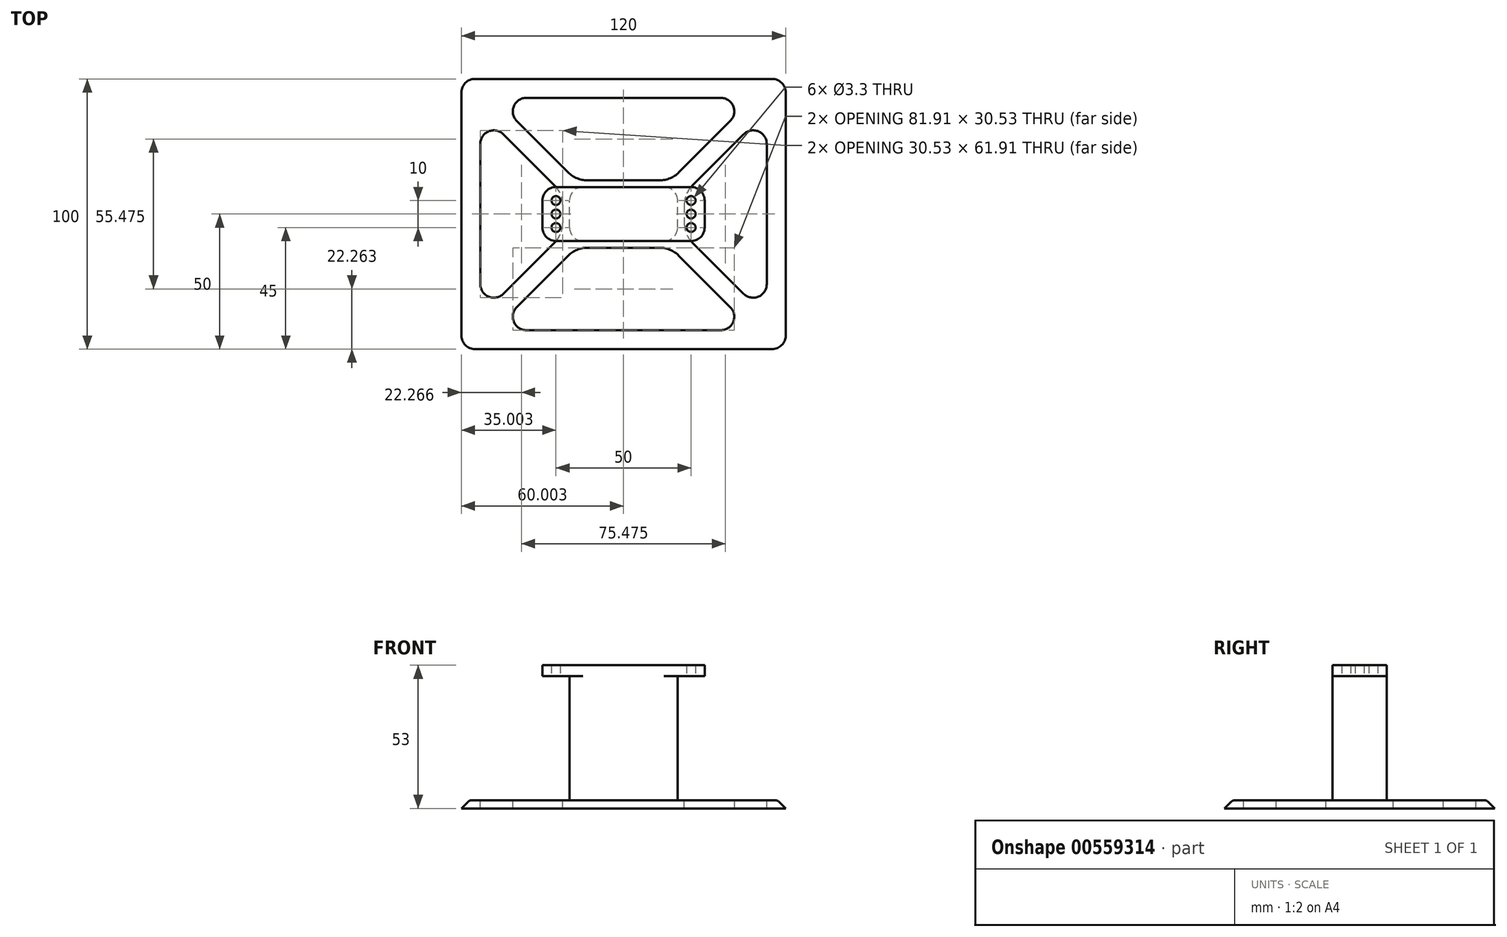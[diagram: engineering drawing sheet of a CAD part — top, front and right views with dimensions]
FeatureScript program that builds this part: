
annotation { "Feature Type Name" : "Feature", "Feature Type Description" : "" }
export const myFeature = defineFeature(function(context is Context, id is Id, definition is map)
    precondition{}
    {
        {
            var Q0;
            Q0=qCreatedBy(makeId("Top.planeOp"),FACE);
            var sketch = newSketch(context, id + "F0", { "sketchPlane" : qUnion([Q0])});
            skLineSegment(sketch, "E0", {"start": v(-14.27, 5) * mm, "end": v(35.73, 5) * mm, "construction": true});
            skLineSegment(sketch, "E1", {"start": v(35.73, 5) * mm, "end": v(35.73, 0) * mm});
            skLineSegment(sketch, "E2", {"start": v(35.73, 5) * mm, "end": v(35.73, 10) * mm});
            skLineSegment(sketch, "E3", {"start": v(-14.27, 5) * mm, "end": v(-14.27, 10) * mm});
            skLineSegment(sketch, "E4", {"start": v(-14.27, 5) * mm, "end": v(-14.27, 0) * mm});
            skLineSegment(sketch, "E5", {"start": v(-14.27, 0) * mm, "end": v(-19.27, 0) * mm, "construction": true});
            skLineSegment(sketch, "E6", {"start": v(35.73, 10) * mm, "end": v(35.73, 15) * mm, "construction": true});
            skLineSegment(sketch, "E7", {"start": v(35.73, 10) * mm, "end": v(40.73, 10) * mm, "construction": true});
            skLineSegment(sketch, "E8", {"start": v(-14.27, 0) * mm, "end": v(-14.27, -5) * mm, "construction": true});
            skLineSegment(sketch, "E9", {"start": v(-19.27, -5) * mm, "end": v(-19.27, 15) * mm});
            skLineSegment(sketch, "E10", {"start": v(-19.27, 15) * mm, "end": v(40.73, 15) * mm});
            skLineSegment(sketch, "E11", {"start": v(40.73, 15) * mm, "end": v(40.73, -5) * mm});
            skLineSegment(sketch, "E12", {"start": v(40.73, -5) * mm, "end": v(-19.27, -5) * mm});
            skCircle(sketch, "E13", {"center": v(-14.27, 10) * mm, "radius": 1.65 * mm});
            skCircle(sketch, "E14", {"center": v(-14.27, 5) * mm, "radius": 1.65 * mm});
            skCircle(sketch, "E15", {"center": v(-14.27, 0) * mm, "radius": 1.65 * mm});
            skCircle(sketch, "E16", {"center": v(35.73, 5) * mm, "radius": 1.65 * mm});
            skCircle(sketch, "E17", {"center": v(35.73, 10) * mm, "radius": 1.65 * mm});
            skCircle(sketch, "E18", {"center": v(35.73, 0) * mm, "radius": 1.65 * mm});
            skSolve(sketch);
        }
        {
            var Q0;
            Q0=makeQuery(id+"F0.imprint","IMPRINT",FACE,{"disambiguationData":[TD([[makeQuery(id+"F0.imprint","IMPRINT",EDGE,{"derivedFrom":sQuery(id+"F0.wireOp",EDGE,"E9")}),-1.0]])]});
            extrude(context, id + "F1", {"entities" : qUnion([Q0]), "depth" : 4 * mm, "offsetDistance" : 25 * mm});
        }
        {
            var Q0;
            Q0=makeQuery(id+"F1.opExtrude","CAP_FACE",FACE,{"disambiguationData":[OSD([sQuery(id+"F0.wireOp",EDGE,"E9"),sQuery(id+"F0.wireOp",EDGE,"E10"),sQuery(id+"F0.wireOp",EDGE,"E11"),sQuery(id+"F0.wireOp",EDGE,"E12"),sQuery(id+"F0.wireOp",EDGE,"E13"),sQuery(id+"F0.wireOp",EDGE,"E14"),sQuery(id+"F0.wireOp",EDGE,"E15"),sQuery(id+"F0.wireOp",EDGE,"E16"),sQuery(id+"F0.wireOp",EDGE,"E17"),sQuery(id+"F0.wireOp",EDGE,"E18")])],"isStart":true});
            var sketch = newSketch(context, id + "F2", { "sketchPlane" : qUnion([Q0])});
            skLineSegment(sketch, "E19", {"start": v(-14.27, 0) * mm, "end": v(-9.27, 0) * mm});
            skLineSegment(sketch, "E20", {"start": v(-9.27, 5) * mm, "end": v(-9.27, -15) * mm});
            skLineSegment(sketch, "E21", {"start": v(35.73, -10) * mm, "end": v(30.73, -10) * mm});
            skLineSegment(sketch, "E22", {"start": v(30.73, 5) * mm, "end": v(30.73, -15) * mm});
            skLineSegment(sketch, "E23", {"start": v(30.73, -15) * mm, "end": v(-9.27, -15) * mm});
            skLineSegment(sketch, "E24", {"start": v(-9.27, 5) * mm, "end": v(30.73, 5) * mm});
            skSolve(sketch);
        }
        {
            var Q0;
            Q0 = qSketchRegion(id + "F2", true);
            var Q1;
            {var subQ2=sQuery(id+"F2.wireOp",EDGE,"E23");Q1=makeQuery(id+"F2.imprint","IMPRINT",FACE,{"disambiguationData":[TD([[makeQuery(id+"F2.imprint","IMPRINT",EDGE,{"derivedFrom":subQ2}),1.0]])]});}
            extrude(context, id + "F3", {"entities" : qUnion([Q0, Q1]), "operationType" : NewBodyOperationType.ADD, "depth" : 46 * mm, "offsetDistance" : 25 * mm});
        }
        {
            var Q0;
            Q0=makeQuery(id+"F3.opExtrude","CAP_FACE",FACE,{"disambiguationData":[OSD([sQuery(id+"F2.wireOp",EDGE,"E20"),sQuery(id+"F2.wireOp",EDGE,"E22"),sQuery(id+"F2.wireOp",EDGE,"E23"),sQuery(id+"F2.wireOp",EDGE,"E24")])],"isStart":false});
            var sketch = newSketch(context, id + "F4", { "sketchPlane" : qUnion([Q0])});
            skLineSegment(sketch, "E25", {"start": v(30.73, 5) * mm, "end": v(70.73, 45) * mm, "construction": true});
            skLineSegment(sketch, "E26", {"start": v(10.73, 5) * mm, "end": v(10.73, -15) * mm, "construction": true});
            skLineSegment(sketch, "E27", {"start": v(30.73, -15) * mm, "end": v(70.73, -55) * mm, "construction": true});
            skLineSegment(sketch, "E28", {"start": v(70.73, 45) * mm, "end": v(70.73, -55) * mm});
            skLineSegment(sketch, "E29", {"start": v(30.73, 5) * mm, "end": v(28.26, 7.47) * mm});
            skLineSegment(sketch, "E30", {"start": v(30.73, 5) * mm, "end": v(33.2, 2.53) * mm});
            skLineSegment(sketch, "E31", {"start": v(33.2, 2.53) * mm, "end": v(70.73, 40.05) * mm});
            skLineSegment(sketch, "E32", {"start": v(30.73, -15) * mm, "end": v(33.2, -12.53) * mm});
            skLineSegment(sketch, "E33", {"start": v(30.73, -15) * mm, "end": v(28.26, -17.47) * mm});
            skLineSegment(sketch, "E34", {"start": v(33.2, -12.53) * mm, "end": v(70.73, -50.05) * mm});
            skLineSegment(sketch, "E35", {"start": v(28.26, -17.47) * mm, "end": v(65.78, -55) * mm});
            skLineSegment(sketch, "E36", {"start": v(28.26, 7.47) * mm, "end": v(65.78, 45) * mm});
            skLineSegment(sketch, "E37", {"start": v(63.73, 33.05) * mm, "end": v(70.73, 33.05) * mm, "construction": true});
            skLineSegment(sketch, "E38", {"start": v(63.73, 33.05) * mm, "end": v(63.73, -43.05) * mm});
            skLineSegment(sketch, "E39.MirrorCS", {"start": v(-9.27, -15) * mm, "end": v(-11.74, -12.53) * mm});
            skLineSegment(sketch, "E40.MirrorCS", {"start": v(-9.27, 5) * mm, "end": v(-11.74, 2.53) * mm});
            skLineSegment(sketch, "E41.MirrorCS", {"start": v(-9.27, -15) * mm, "end": v(-6.8, -17.47) * mm});
            skLineSegment(sketch, "E42.MirrorCS", {"start": v(-9.27, 5) * mm, "end": v(-6.8, 7.47) * mm});
            skLineSegment(sketch, "E43.MirrorCS", {"start": v(-42.27, 33.05) * mm, "end": v(-49.27, 33.05) * mm, "construction": true});
            skLineSegment(sketch, "E44.MirrorCS", {"start": v(-49.27, 45) * mm, "end": v(-49.27, -55) * mm});
            skLineSegment(sketch, "E45.MirrorCS", {"start": v(-6.8, 7.47) * mm, "end": v(-44.32, 45) * mm});
            skLineSegment(sketch, "E46.MirrorCS", {"start": v(-9.27, -15) * mm, "end": v(-49.27, -55) * mm, "construction": true});
            skLineSegment(sketch, "E47.MirrorCS", {"start": v(-11.74, -12.53) * mm, "end": v(-49.27, -50.05) * mm});
            skLineSegment(sketch, "E48.MirrorCS", {"start": v(-9.27, 5) * mm, "end": v(-49.27, 45) * mm, "construction": true});
            skLineSegment(sketch, "E49.MirrorCS", {"start": v(-6.8, -17.47) * mm, "end": v(-44.32, -55) * mm});
            skLineSegment(sketch, "E50.MirrorCS", {"start": v(-42.27, 33.05) * mm, "end": v(-42.27, -43.05) * mm});
            skLineSegment(sketch, "E51.MirrorCS", {"start": v(-11.74, 2.53) * mm, "end": v(-49.27, 40.05) * mm});
            skLineSegment(sketch, "E52", {"start": v(70.73, 45) * mm, "end": v(-49.27, 45) * mm});
            skLineSegment(sketch, "E53", {"start": v(-49.27, -55) * mm, "end": v(70.73, -55) * mm});
            skLineSegment(sketch, "E54", {"start": v(-6.8, 7.47) * mm, "end": v(28.26, 7.47) * mm});
            skLineSegment(sketch, "E55", {"start": v(28.26, -17.47) * mm, "end": v(-6.8, -17.47) * mm});
            skLineSegment(sketch, "E56", {"start": v(-11.74, -12.53) * mm, "end": v(-11.74, 2.53) * mm});
            skLineSegment(sketch, "E57", {"start": v(33.2, -12.53) * mm, "end": v(33.2, 2.53) * mm});
            skLineSegment(sketch, "E58", {"start": v(-37.32, 38) * mm, "end": v(-37.32, 45) * mm});
            skLineSegment(sketch, "E59", {"start": v(58.78, -55) * mm, "end": v(58.78, -48) * mm});
            skLineSegment(sketch, "E60", {"start": v(58.78, -48) * mm, "end": v(-37.32, -48) * mm});
            skLineSegment(sketch, "E61", {"start": v(-37.32, 38) * mm, "end": v(58.78, 38) * mm});
            skSolve(sketch);
        }
        {
            var Q0;
            Q0 = qSketchRegion(id + "F4", true);
            var Q1;
            Q1=makeQuery(id+"F4.imprint","IMPRINT",FACE,{"disambiguationData":[TD([[makeQuery(id+"F4.imprint","IMPRINT",EDGE,{"derivedFrom":makeQuery(id+"F3.opExtrude","CAP_EDGE",EDGE,{"disambiguationData":[OSD([sQuery(id+"F2.wireOp",EDGE,"E20")])],"isStart":false})}),1.0]])]});
            var Q2;
            Q2=makeQuery(id+"F4.imprint","IMPRINT",FACE,{"disambiguationData":[TD([[makeQuery(id+"F4.imprint","IMPRINT",EDGE,{"derivedFrom":sQuery(id+"F4.wireOp",EDGE,"E29")}),1.0]])]});
            var Q3;
            Q3=makeQuery(id+"F4.imprint","IMPRINT",FACE,{"disambiguationData":[TD([[makeQuery(id+"F4.imprint","IMPRINT",EDGE,{"derivedFrom":sQuery(id+"F4.wireOp",EDGE,"E33")}),-1.0]])]});
            var Q4;
            Q4=makeQuery(id+"F4.imprint","IMPRINT",FACE,{"disambiguationData":[TD([[makeQuery(id+"F4.imprint","IMPRINT",EDGE,{"derivedFrom":sQuery(id+"F4.wireOp",EDGE,"E39.MirrorCS")}),-1.0]])]});
            var Q5;
            Q5=makeQuery(id+"F4.imprint","IMPRINT",FACE,{"disambiguationData":[TD([[makeQuery(id+"F4.imprint","IMPRINT",EDGE,{"derivedFrom":sQuery(id+"F4.wireOp",EDGE,"E30")}),-1.0]])]});
            extrude(context, id + "F5", {"entities" : qUnion([Q0, Q1, Q2, Q3, Q4, Q5]), "operationType" : NewBodyOperationType.ADD, "depth" : 3 * mm, "offsetDistance" : 25 * mm});
        }
        {
            var Q0;
            Q0=makeQuery(id+"F3.opExtrude","CAP_EDGE",EDGE,{"disambiguationData":[OSD([sQuery(id+"F2.wireOp",EDGE,"E23")])],"isStart":false});
            var Q1;
            Q1=makeQuery(id+"F3.opExtrude","CAP_EDGE",EDGE,{"disambiguationData":[OSD([sQuery(id+"F2.wireOp",EDGE,"E22")])],"isStart":false});
            var Q2;
            Q2=makeQuery(id+"F3.opExtrude","CAP_EDGE",EDGE,{"disambiguationData":[OSD([sQuery(id+"F2.wireOp",EDGE,"E20")])],"isStart":false});
            var Q3;
            Q3=makeQuery(id+"F3.opExtrude","CAP_EDGE",EDGE,{"disambiguationData":[OSD([sQuery(id+"F2.wireOp",EDGE,"E24")])],"isStart":false});
            var Q4;
            Q4=makeQuery(id+"F1.opExtrude","SWEPT_EDGE",EDGE,{"disambiguationData":[OSD([sQuery(id+"F0.wireOp",EDGE,"E11"),sQuery(id+"F0.wireOp",EDGE,"E12")])]});
            var Q5;
            Q5=makeQuery(id+"F1.opExtrude","SWEPT_EDGE",EDGE,{"disambiguationData":[OSD([sQuery(id+"F0.wireOp",EDGE,"E10"),sQuery(id+"F0.wireOp",EDGE,"E11")])]});
            var Q6;
            Q6=makeQuery(id+"F1.opExtrude","SWEPT_EDGE",EDGE,{"disambiguationData":[OSD([sQuery(id+"F0.wireOp",EDGE,"E9"),sQuery(id+"F0.wireOp",EDGE,"E10")])]});
            var Q7;
            Q7=makeQuery(id+"F1.opExtrude","SWEPT_EDGE",EDGE,{"disambiguationData":[OSD([sQuery(id+"F0.wireOp",EDGE,"E9"),sQuery(id+"F0.wireOp",EDGE,"E12")])]});
            var Q8;
            Q8=makeQuery(id+"F5.opExtrude","SWEPT_EDGE",EDGE,{"disambiguationData":[OSD([sQuery(id+"F4.wireOp",EDGE,"E44.MirrorCS"),sQuery(id+"F4.wireOp",EDGE,"E52")])]});
            var Q9;
            Q9=makeQuery(id+"F5.opExtrude","SWEPT_EDGE",EDGE,{"disambiguationData":[OSD([sQuery(id+"F4.wireOp",EDGE,"E44.MirrorCS"),sQuery(id+"F4.wireOp",EDGE,"E53")])]});
            var Q10;
            Q10=makeQuery(id+"F5.opExtrude","SWEPT_EDGE",EDGE,{"disambiguationData":[OSD([sQuery(id+"F4.wireOp",EDGE,"E28"),sQuery(id+"F4.wireOp",EDGE,"E53")])]});
            var Q11;
            Q11=makeQuery(id+"F5.opExtrude","SWEPT_EDGE",EDGE,{"disambiguationData":[OSD([sQuery(id+"F4.wireOp",EDGE,"E28"),sQuery(id+"F4.wireOp",EDGE,"E52")])]});
            fillet(context, id + "F6", {"entities" : qUnion([Q0, Q1, Q2, Q3, Q4, Q5, Q6, Q7, Q8, Q9, Q10, Q11]), "radius" : 5 * mm, "tangentPropagation" : true, "allowEdgeOverflow" : false});
        }
        {
            var Q0;
            Q0=makeQuery(id+"F3.opExtrude","SWEPT_EDGE",EDGE,{"disambiguationData":[OSD([sQuery(id+"F0.wireOp",EDGE,"E10"),sQuery(id+"F2.wireOp",EDGE,"E20"),sQuery(id+"F2.wireOp",EDGE,"E23")])]});
            var Q1;
            Q1=makeQuery(id+"F3.opExtrude","SWEPT_EDGE",EDGE,{"disambiguationData":[OSD([sQuery(id+"F0.wireOp",EDGE,"E10"),sQuery(id+"F2.wireOp",EDGE,"E22"),sQuery(id+"F2.wireOp",EDGE,"E23")])]});
            var Q2;
            Q2=makeQuery(id+"F3.opExtrude","SWEPT_EDGE",EDGE,{"disambiguationData":[OSD([sQuery(id+"F0.wireOp",EDGE,"E12"),sQuery(id+"F2.wireOp",EDGE,"E22"),sQuery(id+"F2.wireOp",EDGE,"E24")])]});
            var Q3;
            Q3=makeQuery(id+"F3.opExtrude","SWEPT_EDGE",EDGE,{"disambiguationData":[OSD([sQuery(id+"F0.wireOp",EDGE,"E12"),sQuery(id+"F2.wireOp",EDGE,"E20"),sQuery(id+"F2.wireOp",EDGE,"E24")])]});
            fillet(context, id + "F7", {"entities" : qUnion([Q0, Q1, Q2, Q3]), "radius" : 5 * mm, "tangentPropagation" : true, "allowEdgeOverflow" : false});
        }
        {
            var Q0;
            Q0=makeQuery(id+"F5.opExtrude","CAP_EDGE",EDGE,{"disambiguationData":[OSD([sQuery(id+"F4.wireOp",EDGE,"E44.MirrorCS")])],"isStart":true});
            chamfer(context, id + "F8", {"entities" : qUnion([Q0]), "width" : 3 * mm, "tangentPropagation" : true});
        }
        {
            var Q0;
            {var subQ0=sQuery(id+"F4.wireOp",EDGE,"E52");Q0=makeQuery(id+"F8.opChamfer","BLEND_EDGE",EDGE,{"blendedFrom":[makeQuery(id+"F5.opExtrude","CAP_EDGE",EDGE,{"disambiguationData":[OSD([subQ0])],"isStart":true}),makeQuery(id+"F5.opExtrude","CAP_FACE",FACE,{"disambiguationData":[OSD([sQuery(id+"F4.wireOp",EDGE,"E28"),sQuery(id+"F4.wireOp",EDGE,"E31"),sQuery(id+"F4.wireOp",EDGE,"E34"),sQuery(id+"F4.wireOp",EDGE,"E35"),sQuery(id+"F4.wireOp",EDGE,"E36"),sQuery(id+"F4.wireOp",EDGE,"E38"),sQuery(id+"F4.wireOp",EDGE,"E44.MirrorCS"),sQuery(id+"F4.wireOp",EDGE,"E45.MirrorCS"),sQuery(id+"F4.wireOp",EDGE,"E47.MirrorCS"),sQuery(id+"F4.wireOp",EDGE,"E49.MirrorCS"),sQuery(id+"F4.wireOp",EDGE,"E50.MirrorCS"),sQuery(id+"F4.wireOp",EDGE,"E51.MirrorCS"),subQ0,sQuery(id+"F4.wireOp",EDGE,"E53"),sQuery(id+"F4.wireOp",EDGE,"E54"),sQuery(id+"F4.wireOp",EDGE,"E55"),sQuery(id+"F4.wireOp",EDGE,"E56"),sQuery(id+"F4.wireOp",EDGE,"E57"),sQuery(id+"F4.wireOp",EDGE,"E60"),sQuery(id+"F4.wireOp",EDGE,"E61")])],"isStart":true})],"blendedInto":[makeQuery(id+"F5.opExtrude","CAP_FACE",FACE,{"disambiguationData":[OSD([sQuery(id+"F4.wireOp",EDGE,"E28"),sQuery(id+"F4.wireOp",EDGE,"E31"),sQuery(id+"F4.wireOp",EDGE,"E34"),sQuery(id+"F4.wireOp",EDGE,"E35"),sQuery(id+"F4.wireOp",EDGE,"E36"),sQuery(id+"F4.wireOp",EDGE,"E38"),sQuery(id+"F4.wireOp",EDGE,"E44.MirrorCS"),sQuery(id+"F4.wireOp",EDGE,"E45.MirrorCS"),sQuery(id+"F4.wireOp",EDGE,"E47.MirrorCS"),sQuery(id+"F4.wireOp",EDGE,"E49.MirrorCS"),sQuery(id+"F4.wireOp",EDGE,"E50.MirrorCS"),sQuery(id+"F4.wireOp",EDGE,"E51.MirrorCS"),subQ0,sQuery(id+"F4.wireOp",EDGE,"E53"),sQuery(id+"F4.wireOp",EDGE,"E54"),sQuery(id+"F4.wireOp",EDGE,"E55"),sQuery(id+"F4.wireOp",EDGE,"E56"),sQuery(id+"F4.wireOp",EDGE,"E57"),sQuery(id+"F4.wireOp",EDGE,"E60"),sQuery(id+"F4.wireOp",EDGE,"E61")])],"isStart":true})]});}
            var Q1;
            {var subQ0=sQuery(id+"F4.wireOp",EDGE,"E28");Q1=makeQuery(id+"F8.opChamfer","BLEND_EDGE",EDGE,{"blendedFrom":[makeQuery(id+"F5.opExtrude","CAP_EDGE",EDGE,{"disambiguationData":[OSD([subQ0])],"isStart":true}),makeQuery(id+"F5.opExtrude","CAP_FACE",FACE,{"disambiguationData":[OSD([subQ0,sQuery(id+"F4.wireOp",EDGE,"E31"),sQuery(id+"F4.wireOp",EDGE,"E34"),sQuery(id+"F4.wireOp",EDGE,"E35"),sQuery(id+"F4.wireOp",EDGE,"E36"),sQuery(id+"F4.wireOp",EDGE,"E38"),sQuery(id+"F4.wireOp",EDGE,"E44.MirrorCS"),sQuery(id+"F4.wireOp",EDGE,"E45.MirrorCS"),sQuery(id+"F4.wireOp",EDGE,"E47.MirrorCS"),sQuery(id+"F4.wireOp",EDGE,"E49.MirrorCS"),sQuery(id+"F4.wireOp",EDGE,"E50.MirrorCS"),sQuery(id+"F4.wireOp",EDGE,"E51.MirrorCS"),sQuery(id+"F4.wireOp",EDGE,"E52"),sQuery(id+"F4.wireOp",EDGE,"E53"),sQuery(id+"F4.wireOp",EDGE,"E54"),sQuery(id+"F4.wireOp",EDGE,"E55"),sQuery(id+"F4.wireOp",EDGE,"E56"),sQuery(id+"F4.wireOp",EDGE,"E57"),sQuery(id+"F4.wireOp",EDGE,"E60"),sQuery(id+"F4.wireOp",EDGE,"E61")])],"isStart":true})],"blendedInto":[makeQuery(id+"F5.opExtrude","CAP_FACE",FACE,{"disambiguationData":[OSD([subQ0,sQuery(id+"F4.wireOp",EDGE,"E31"),sQuery(id+"F4.wireOp",EDGE,"E34"),sQuery(id+"F4.wireOp",EDGE,"E35"),sQuery(id+"F4.wireOp",EDGE,"E36"),sQuery(id+"F4.wireOp",EDGE,"E38"),sQuery(id+"F4.wireOp",EDGE,"E44.MirrorCS"),sQuery(id+"F4.wireOp",EDGE,"E45.MirrorCS"),sQuery(id+"F4.wireOp",EDGE,"E47.MirrorCS"),sQuery(id+"F4.wireOp",EDGE,"E49.MirrorCS"),sQuery(id+"F4.wireOp",EDGE,"E50.MirrorCS"),sQuery(id+"F4.wireOp",EDGE,"E51.MirrorCS"),sQuery(id+"F4.wireOp",EDGE,"E52"),sQuery(id+"F4.wireOp",EDGE,"E53"),sQuery(id+"F4.wireOp",EDGE,"E54"),sQuery(id+"F4.wireOp",EDGE,"E55"),sQuery(id+"F4.wireOp",EDGE,"E56"),sQuery(id+"F4.wireOp",EDGE,"E57"),sQuery(id+"F4.wireOp",EDGE,"E60"),sQuery(id+"F4.wireOp",EDGE,"E61")])],"isStart":true})]});}
            var Q2;
            {var subQ0=sQuery(id+"F4.wireOp",EDGE,"E52");var subQ1=sQuery(id+"F4.wireOp",EDGE,"E28");var subQ2=makeQuery(id+"F5.opExtrude","CAP_FACE",FACE,{"disambiguationData":[OSD([subQ1,sQuery(id+"F4.wireOp",EDGE,"E31"),sQuery(id+"F4.wireOp",EDGE,"E34"),sQuery(id+"F4.wireOp",EDGE,"E35"),sQuery(id+"F4.wireOp",EDGE,"E36"),sQuery(id+"F4.wireOp",EDGE,"E38"),sQuery(id+"F4.wireOp",EDGE,"E44.MirrorCS"),sQuery(id+"F4.wireOp",EDGE,"E45.MirrorCS"),sQuery(id+"F4.wireOp",EDGE,"E47.MirrorCS"),sQuery(id+"F4.wireOp",EDGE,"E49.MirrorCS"),sQuery(id+"F4.wireOp",EDGE,"E50.MirrorCS"),sQuery(id+"F4.wireOp",EDGE,"E51.MirrorCS"),subQ0,sQuery(id+"F4.wireOp",EDGE,"E53"),sQuery(id+"F4.wireOp",EDGE,"E54"),sQuery(id+"F4.wireOp",EDGE,"E55"),sQuery(id+"F4.wireOp",EDGE,"E56"),sQuery(id+"F4.wireOp",EDGE,"E57"),sQuery(id+"F4.wireOp",EDGE,"E60"),sQuery(id+"F4.wireOp",EDGE,"E61")])],"isStart":true});Q2=makeQuery(id+"F8.opChamfer","BLEND_EDGE",EDGE,{"blendedFrom":[makeQuery(id+"F6.opFillet","BLEND_EDGE",EDGE,{"blendedFrom":[makeQuery(id+"F5.opExtrude","SWEPT_EDGE",EDGE,{"disambiguationData":[OSD([subQ1,subQ0])]}),subQ2],"blendedInto":[subQ2]}),subQ2],"blendedInto":[subQ2]});}
            var Q3;
            {var subQ0=sQuery(id+"F4.wireOp",EDGE,"E44.MirrorCS");Q3=makeQuery(id+"F8.opChamfer","BLEND_EDGE",EDGE,{"blendedFrom":[makeQuery(id+"F5.opExtrude","CAP_EDGE",EDGE,{"disambiguationData":[OSD([subQ0])],"isStart":true}),makeQuery(id+"F5.opExtrude","CAP_FACE",FACE,{"disambiguationData":[OSD([sQuery(id+"F4.wireOp",EDGE,"E28"),sQuery(id+"F4.wireOp",EDGE,"E31"),sQuery(id+"F4.wireOp",EDGE,"E34"),sQuery(id+"F4.wireOp",EDGE,"E35"),sQuery(id+"F4.wireOp",EDGE,"E36"),sQuery(id+"F4.wireOp",EDGE,"E38"),subQ0,sQuery(id+"F4.wireOp",EDGE,"E45.MirrorCS"),sQuery(id+"F4.wireOp",EDGE,"E47.MirrorCS"),sQuery(id+"F4.wireOp",EDGE,"E49.MirrorCS"),sQuery(id+"F4.wireOp",EDGE,"E50.MirrorCS"),sQuery(id+"F4.wireOp",EDGE,"E51.MirrorCS"),sQuery(id+"F4.wireOp",EDGE,"E52"),sQuery(id+"F4.wireOp",EDGE,"E53"),sQuery(id+"F4.wireOp",EDGE,"E54"),sQuery(id+"F4.wireOp",EDGE,"E55"),sQuery(id+"F4.wireOp",EDGE,"E56"),sQuery(id+"F4.wireOp",EDGE,"E57"),sQuery(id+"F4.wireOp",EDGE,"E60"),sQuery(id+"F4.wireOp",EDGE,"E61")])],"isStart":true})],"blendedInto":[makeQuery(id+"F5.opExtrude","CAP_FACE",FACE,{"disambiguationData":[OSD([sQuery(id+"F4.wireOp",EDGE,"E28"),sQuery(id+"F4.wireOp",EDGE,"E31"),sQuery(id+"F4.wireOp",EDGE,"E34"),sQuery(id+"F4.wireOp",EDGE,"E35"),sQuery(id+"F4.wireOp",EDGE,"E36"),sQuery(id+"F4.wireOp",EDGE,"E38"),subQ0,sQuery(id+"F4.wireOp",EDGE,"E45.MirrorCS"),sQuery(id+"F4.wireOp",EDGE,"E47.MirrorCS"),sQuery(id+"F4.wireOp",EDGE,"E49.MirrorCS"),sQuery(id+"F4.wireOp",EDGE,"E50.MirrorCS"),sQuery(id+"F4.wireOp",EDGE,"E51.MirrorCS"),sQuery(id+"F4.wireOp",EDGE,"E52"),sQuery(id+"F4.wireOp",EDGE,"E53"),sQuery(id+"F4.wireOp",EDGE,"E54"),sQuery(id+"F4.wireOp",EDGE,"E55"),sQuery(id+"F4.wireOp",EDGE,"E56"),sQuery(id+"F4.wireOp",EDGE,"E57"),sQuery(id+"F4.wireOp",EDGE,"E60"),sQuery(id+"F4.wireOp",EDGE,"E61")])],"isStart":true})]});}
            var Q4;
            {var subQ0=sQuery(id+"F4.wireOp",EDGE,"E52");var subQ1=sQuery(id+"F4.wireOp",EDGE,"E44.MirrorCS");var subQ2=makeQuery(id+"F5.opExtrude","CAP_FACE",FACE,{"disambiguationData":[OSD([sQuery(id+"F4.wireOp",EDGE,"E28"),sQuery(id+"F4.wireOp",EDGE,"E31"),sQuery(id+"F4.wireOp",EDGE,"E34"),sQuery(id+"F4.wireOp",EDGE,"E35"),sQuery(id+"F4.wireOp",EDGE,"E36"),sQuery(id+"F4.wireOp",EDGE,"E38"),subQ1,sQuery(id+"F4.wireOp",EDGE,"E45.MirrorCS"),sQuery(id+"F4.wireOp",EDGE,"E47.MirrorCS"),sQuery(id+"F4.wireOp",EDGE,"E49.MirrorCS"),sQuery(id+"F4.wireOp",EDGE,"E50.MirrorCS"),sQuery(id+"F4.wireOp",EDGE,"E51.MirrorCS"),subQ0,sQuery(id+"F4.wireOp",EDGE,"E53"),sQuery(id+"F4.wireOp",EDGE,"E54"),sQuery(id+"F4.wireOp",EDGE,"E55"),sQuery(id+"F4.wireOp",EDGE,"E56"),sQuery(id+"F4.wireOp",EDGE,"E57"),sQuery(id+"F4.wireOp",EDGE,"E60"),sQuery(id+"F4.wireOp",EDGE,"E61")])],"isStart":true});Q4=makeQuery(id+"F8.opChamfer","BLEND_EDGE",EDGE,{"blendedFrom":[makeQuery(id+"F6.opFillet","BLEND_EDGE",EDGE,{"blendedFrom":[makeQuery(id+"F5.opExtrude","SWEPT_EDGE",EDGE,{"disambiguationData":[OSD([subQ1,subQ0])]}),subQ2],"blendedInto":[subQ2]}),subQ2],"blendedInto":[subQ2]});}
            fillet(context, id + "F9", {"entities" : qUnion([Q0, Q1, Q2, Q3, Q4]), "radius" : 2 * mm, "tangentPropagation" : true, "allowEdgeOverflow" : false});
        }
        {
            var Q0;
            Q0=makeQuery(id+"F5.opExtrude","SWEPT_EDGE",EDGE,{"disambiguationData":[OSD([sQuery(id+"F4.wireOp",EDGE,"E45.MirrorCS"),sQuery(id+"F4.wireOp",EDGE,"E58"),sQuery(id+"F4.wireOp",EDGE,"E61")])]});
            var Q1;
            Q1=makeQuery(id+"F5.opExtrude","SWEPT_EDGE",EDGE,{"disambiguationData":[OSD([sQuery(id+"F4.wireOp",EDGE,"E50.MirrorCS"),sQuery(id+"F4.wireOp",EDGE,"E51.MirrorCS")])]});
            var Q2;
            Q2=makeQuery(id+"F5.opExtrude","SWEPT_EDGE",EDGE,{"disambiguationData":[OSD([sQuery(id+"F4.wireOp",EDGE,"E49.MirrorCS"),sQuery(id+"F4.wireOp",EDGE,"E60")])]});
            var Q3;
            Q3=makeQuery(id+"F5.opExtrude","SWEPT_EDGE",EDGE,{"disambiguationData":[OSD([sQuery(id+"F4.wireOp",EDGE,"E47.MirrorCS"),sQuery(id+"F4.wireOp",EDGE,"E50.MirrorCS")])]});
            var Q4;
            Q4=makeQuery(id+"F5.opExtrude","SWEPT_EDGE",EDGE,{"disambiguationData":[OSD([sQuery(id+"F4.wireOp",EDGE,"E36"),sQuery(id+"F4.wireOp",EDGE,"E61")])]});
            var Q5;
            Q5=makeQuery(id+"F5.opExtrude","SWEPT_EDGE",EDGE,{"disambiguationData":[OSD([sQuery(id+"F4.wireOp",EDGE,"E31"),sQuery(id+"F4.wireOp",EDGE,"E38")])]});
            var Q6;
            Q6=makeQuery(id+"F5.opExtrude","SWEPT_EDGE",EDGE,{"disambiguationData":[OSD([sQuery(id+"F4.wireOp",EDGE,"E35"),sQuery(id+"F4.wireOp",EDGE,"E59"),sQuery(id+"F4.wireOp",EDGE,"E60")])]});
            var Q7;
            Q7=makeQuery(id+"F5.opExtrude","SWEPT_EDGE",EDGE,{"disambiguationData":[OSD([sQuery(id+"F4.wireOp",EDGE,"E34"),sQuery(id+"F4.wireOp",EDGE,"E38")])]});
            fillet(context, id + "F10", {"entities" : qUnion([Q0, Q1, Q2, Q3, Q4, Q5, Q6, Q7]), "radius" : 5 * mm, "tangentPropagation" : true, "allowEdgeOverflow" : false});
        }
        {
            var Q0;
            Q0=makeQuery(id+"F5.opExtrude","SWEPT_EDGE",EDGE,{"disambiguationData":[OSD([sQuery(id+"F4.wireOp",EDGE,"E32"),sQuery(id+"F4.wireOp",EDGE,"E34"),sQuery(id+"F4.wireOp",EDGE,"E57")])]});
            var Q1;
            Q1=makeQuery(id+"F5.opExtrude","SWEPT_EDGE",EDGE,{"disambiguationData":[OSD([sQuery(id+"F4.wireOp",EDGE,"E30"),sQuery(id+"F4.wireOp",EDGE,"E31"),sQuery(id+"F4.wireOp",EDGE,"E57")])]});
            var Q2;
            Q2=makeQuery(id+"F5.opExtrude","SWEPT_EDGE",EDGE,{"disambiguationData":[OSD([sQuery(id+"F4.wireOp",EDGE,"E29"),sQuery(id+"F4.wireOp",EDGE,"E36"),sQuery(id+"F4.wireOp",EDGE,"E54")])]});
            var Q3;
            Q3=makeQuery(id+"F5.opExtrude","SWEPT_EDGE",EDGE,{"disambiguationData":[OSD([sQuery(id+"F4.wireOp",EDGE,"E42.MirrorCS"),sQuery(id+"F4.wireOp",EDGE,"E45.MirrorCS"),sQuery(id+"F4.wireOp",EDGE,"E54")])]});
            var Q4;
            Q4=makeQuery(id+"F5.opExtrude","SWEPT_EDGE",EDGE,{"disambiguationData":[OSD([sQuery(id+"F4.wireOp",EDGE,"E39.MirrorCS"),sQuery(id+"F4.wireOp",EDGE,"E47.MirrorCS"),sQuery(id+"F4.wireOp",EDGE,"E56")])]});
            var Q5;
            Q5=makeQuery(id+"F5.opExtrude","SWEPT_EDGE",EDGE,{"disambiguationData":[OSD([sQuery(id+"F4.wireOp",EDGE,"E40.MirrorCS"),sQuery(id+"F4.wireOp",EDGE,"E51.MirrorCS"),sQuery(id+"F4.wireOp",EDGE,"E56")])]});
            var Q6;
            Q6=makeQuery(id+"F5.opExtrude","SWEPT_EDGE",EDGE,{"disambiguationData":[OSD([sQuery(id+"F4.wireOp",EDGE,"E41.MirrorCS"),sQuery(id+"F4.wireOp",EDGE,"E49.MirrorCS"),sQuery(id+"F4.wireOp",EDGE,"E55")])]});
            var Q7;
            Q7=makeQuery(id+"F5.opExtrude","SWEPT_EDGE",EDGE,{"disambiguationData":[OSD([sQuery(id+"F4.wireOp",EDGE,"E33"),sQuery(id+"F4.wireOp",EDGE,"E35"),sQuery(id+"F4.wireOp",EDGE,"E55")])]});
            fillet(context, id + "F11", {"entities" : qUnion([Q0, Q1, Q2, Q3, Q4, Q5, Q6, Q7]), "radius" : 10 * mm, "tangentPropagation" : true, "allowEdgeOverflow" : false});
        }
    });
